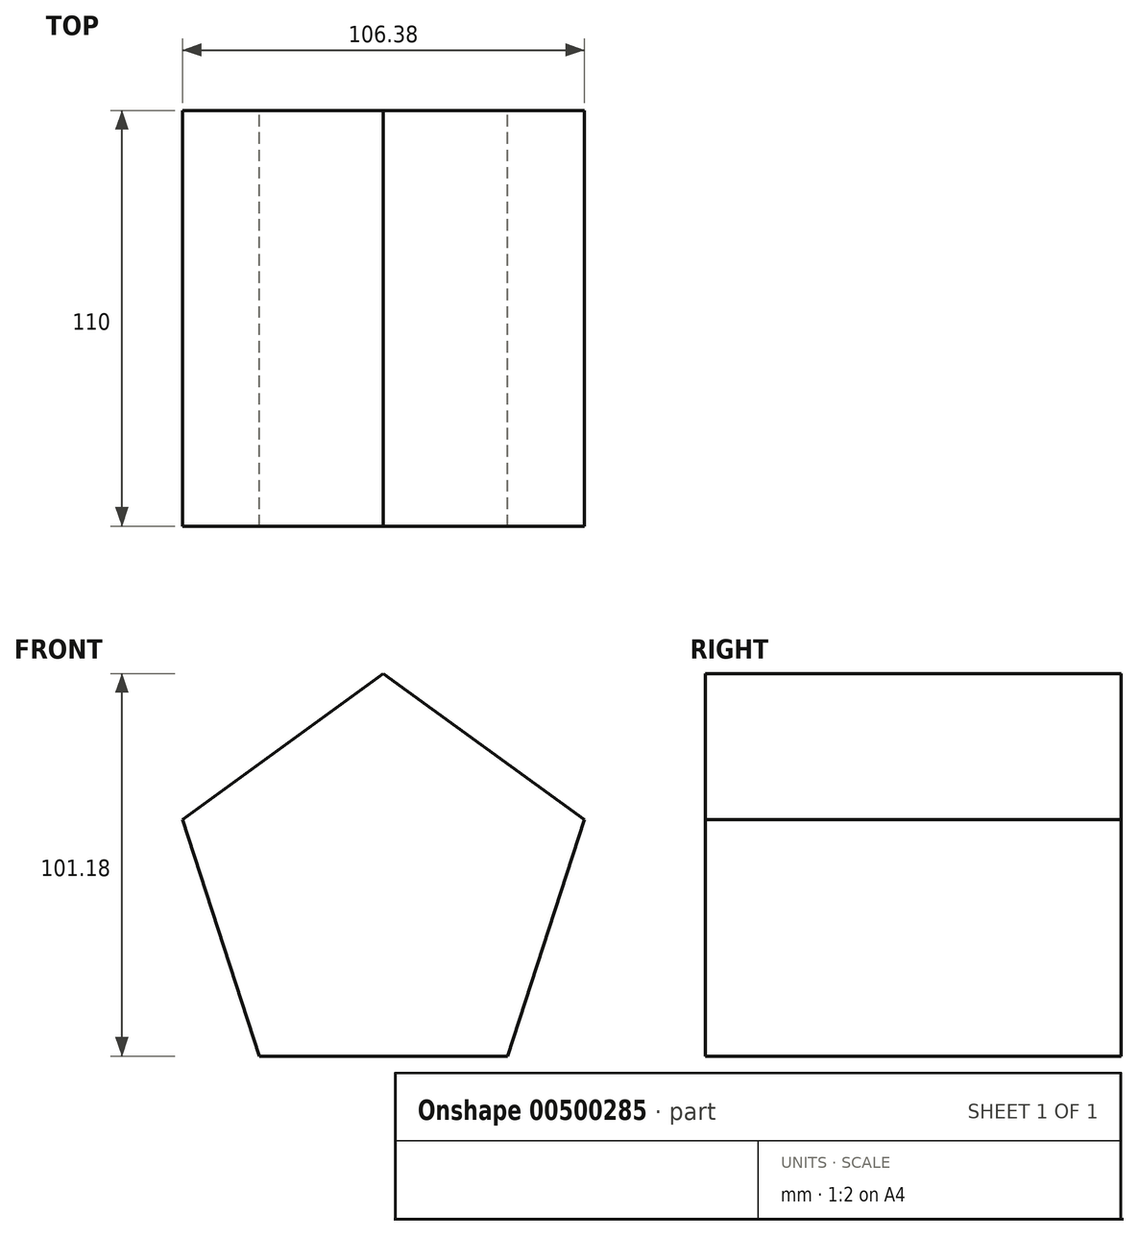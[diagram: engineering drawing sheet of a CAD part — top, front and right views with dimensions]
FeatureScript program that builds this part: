
annotation { "Feature Type Name" : "Feature", "Feature Type Description" : "" }
export const myFeature = defineFeature(function(context is Context, id is Id, definition is map)
    precondition{}
    {
        {
            var Q0;
            Q0=qCreatedBy(makeId("Front.planeOp"),FACE);
            var sketch = newSketch(context, id + "F0", { "sketchPlane" : qUnion([Q0])});
            skCircle(sketch, "E0.cCircle", {"center": v(0, 0) * mm, "radius": 55.93 * mm, "construction": true});
            skLineSegment(sketch, "E0.0", {"start": v(0, 55.93) * mm, "end": v(53.2, 17.28) * mm});
            skLineSegment(sketch, "E0.1", {"start": v(53.2, 17.28) * mm, "end": v(32.88, -45.25) * mm});
            skLineSegment(sketch, "E0.2", {"start": v(32.88, -45.25) * mm, "end": v(-32.88, -45.25) * mm});
            skLineSegment(sketch, "E0.3", {"start": v(-32.88, -45.25) * mm, "end": v(-53.2, 17.28) * mm});
            skLineSegment(sketch, "E0.4", {"start": v(-53.2, 17.28) * mm, "end": v(0, 55.93) * mm});
            skSolve(sketch);
        }
        {
            var Q0;
            Q0=makeQuery(id+"F0.imprint","IMPRINT",FACE,{"disambiguationData":[TD([[makeQuery(id+"F0.imprint","IMPRINT",EDGE,{"derivedFrom":sQuery(id+"F0.wireOp",EDGE,"E0.0")}),-1.0]])]});
            extrude(context, id + "F1", {"entities" : qUnion([Q0]), "depth" : 110 * mm});
        }
    });
